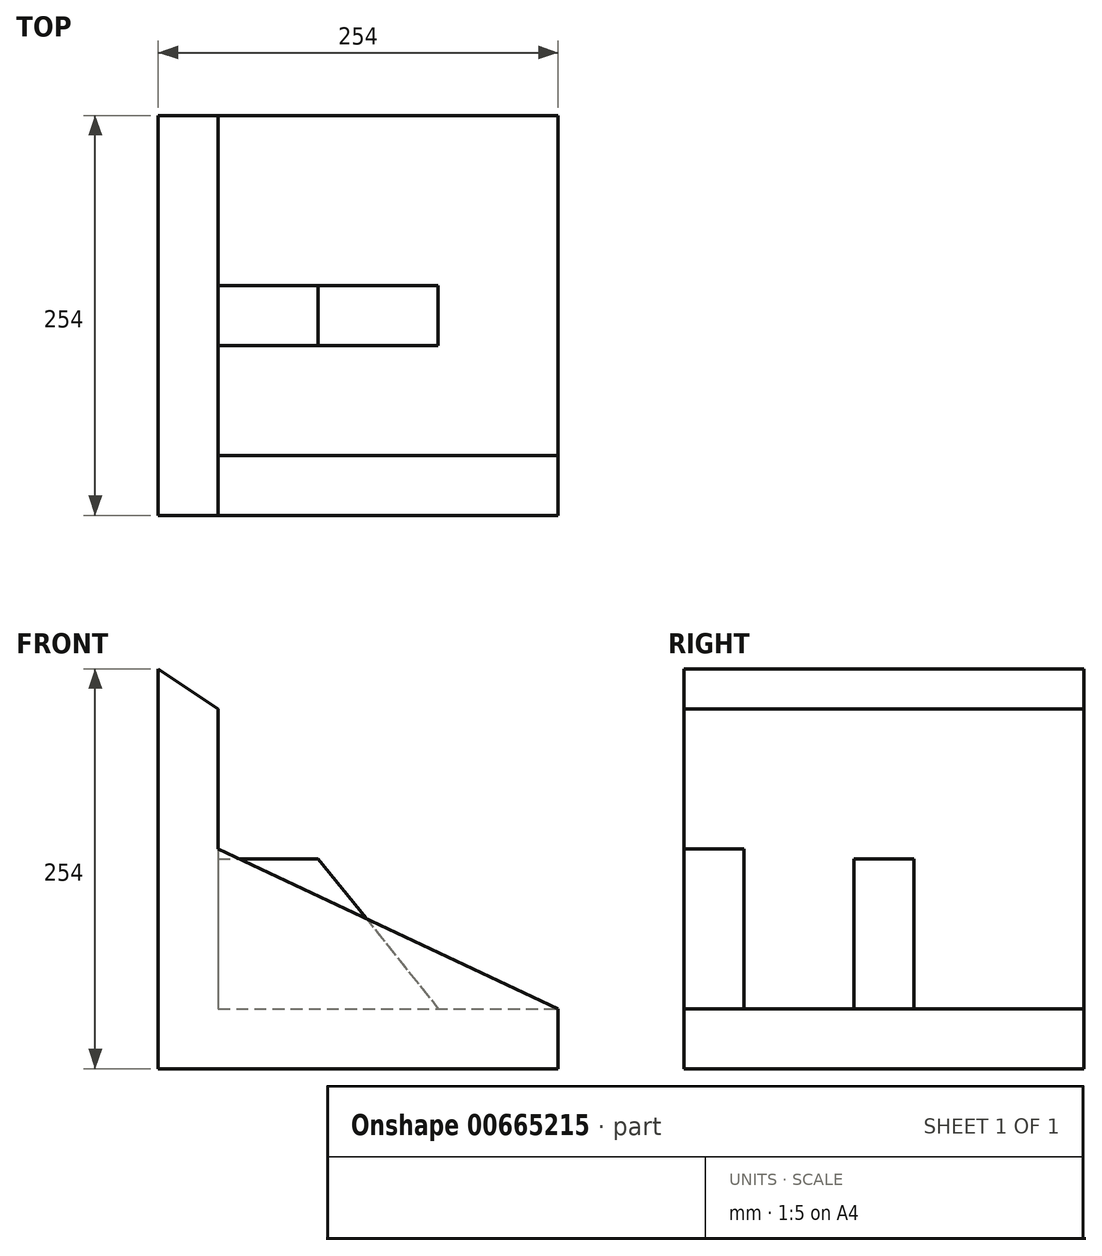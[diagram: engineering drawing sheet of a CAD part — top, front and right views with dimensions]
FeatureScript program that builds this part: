
annotation { "Feature Type Name" : "Feature", "Feature Type Description" : "" }
export const myFeature = defineFeature(function(context is Context, id is Id, definition is map)
    precondition{}
    {
        {
            var Q0;
            Q0=qCreatedBy(makeId("Front.planeOp"),FACE);
            var sketch = newSketch(context, id + "F0", { "sketchPlane" : qUnion([Q0])});
            skLineSegment(sketch, "E0", {"start": v(0, 0) * mm, "end": v(0, 254) * mm});
            skLineSegment(sketch, "E1", {"start": v(0, 0) * mm, "end": v(254, 0) * mm});
            skLineSegment(sketch, "E2", {"start": v(0, 254) * mm, "end": v(38.1, 228.6) * mm});
            skLineSegment(sketch, "E3", {"start": v(38.1, 228.6) * mm, "end": v(38.1, 38.1) * mm});
            skLineSegment(sketch, "E4", {"start": v(38.1, 38.1) * mm, "end": v(254, 38.1) * mm});
            skLineSegment(sketch, "E5", {"start": v(254, 38.1) * mm, "end": v(254, 0) * mm});
            skLineSegment(sketch, "E6", {"start": v(38.1, 133.35) * mm, "end": v(101.6, 133.35) * mm});
            skLineSegment(sketch, "E7", {"start": v(101.6, 133.35) * mm, "end": v(177.8, 38.1) * mm});
            skSolve(sketch);
        }
        {
            var Q0;
            Q0=makeQuery(id+"F0.imprint","IMPRINT",FACE,{"disambiguationData":[TD([[makeQuery(id+"F0.imprint","IMPRINT",EDGE,{"derivedFrom":sQuery(id+"F0.wireOp",EDGE,"E0")}),-1.0]])]});
            extrude(context, id + "F1", {"entities" : qUnion([Q0]), "endBound" : BoundingType.SYMMETRIC, "depth" : 254 * mm, "offsetDistance" : 25.4 * mm});
        }
        {
            var Q0;
            Q0=makeQuery(id+"F1.opExtrude","CAP_FACE",FACE,{"disambiguationData":[OSD([sQuery(id+"F0.wireOp",EDGE,"E0"),sQuery(id+"F0.wireOp",EDGE,"E1"),sQuery(id+"F0.wireOp",EDGE,"E2"),sQuery(id+"F0.wireOp",EDGE,"E3"),sQuery(id+"F0.wireOp",EDGE,"E4"),sQuery(id+"F0.wireOp",EDGE,"E5")])],"isStart":false});
            var sketch = newSketch(context, id + "F2", { "sketchPlane" : qUnion([Q0])});
            skLineSegment(sketch, "E8", {"start": v(38.1, 139.7) * mm, "end": v(254, 38.1) * mm});
            skSolve(sketch);
        }
        {
            var Q0;
            {var subQ0=sQuery(id+"F2.wireOp",EDGE,"E8");Q0=makeQuery(id+"F2.imprint","IMPRINT",FACE,{"disambiguationData":[TD([[makeQuery(id+"F2.imprint","IMPRINT",EDGE,{"derivedFrom":subQ0}),-1.0]])]});}
            extrude(context, id + "F3", {"entities" : qUnion([Q0]), "operationType" : NewBodyOperationType.ADD, "oppositeDirection" : true, "depth" : 38.1 * mm, "offsetDistance" : 25.4 * mm});
        }
        {
            var Q0;
            Q0 = qSketchRegion(id + "F0", true);
            extrude(context, id + "F4", {"entities" : qUnion([Q0]), "operationType" : NewBodyOperationType.ADD, "endBound" : BoundingType.SYMMETRIC, "oppositeDirection" : true, "depth" : 38.1 * mm, "offsetDistance" : 25.4 * mm});
        }
    });
